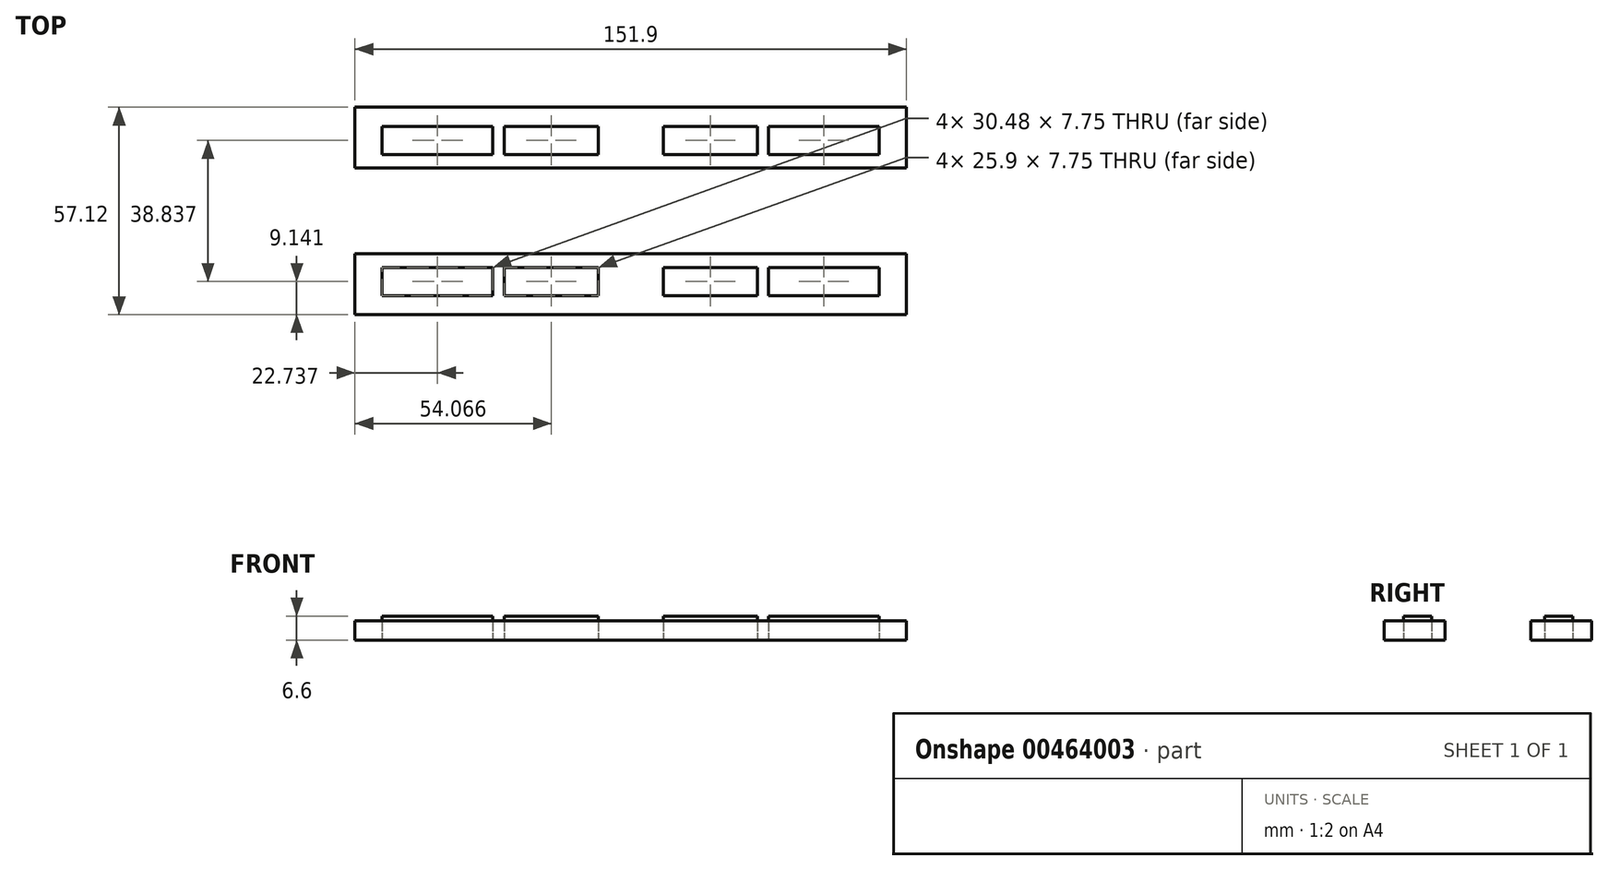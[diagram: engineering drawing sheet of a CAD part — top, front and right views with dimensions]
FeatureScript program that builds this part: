
annotation { "Feature Type Name" : "Feature", "Feature Type Description" : "" }
export const myFeature = defineFeature(function(context is Context, id is Id, definition is map)
    precondition{}
    {
        {
            var Q0;
            Q0=qCreatedBy(makeId("Top.planeOp"),FACE);
            var sketch = newSketch(context, id + "F0", { "sketchPlane" : qUnion([Q0])});
            skLineSegment(sketch, "E0", {"start": v(0, 28.56) * mm, "end": v(-75.95, 28.56) * mm});
            skLineSegment(sketch, "E1", {"start": v(0, 28.56) * mm, "end": v(75.95, 28.56) * mm});
            skLineSegment(sketch, "E2", {"start": v(-75.95, 28.56) * mm, "end": v(-75.95, 11.8) * mm});
            skLineSegment(sketch, "E3.MirrorCS", {"start": v(75.95, 28.56) * mm, "end": v(75.95, 11.8) * mm});
            skLineSegment(sketch, "E4", {"start": v(-75.95, 11.8) * mm, "end": v(0, 11.8) * mm});
            skLineSegment(sketch, "E5", {"start": v(0, 11.8) * mm, "end": v(75.95, 11.8) * mm});
            skLineSegment(sketch, "E6", {"start": v(-68.45, 20.18) * mm, "end": v(-68.45, 23.3) * mm});
            skPoint(sketch, "E6.startSnap0", {"position": v(-75.95, 20.18) * mm});
            skLineSegment(sketch, "E7", {"start": v(-68.45, 23.3) * mm, "end": v(-68.45, 15.54) * mm});
            skLineSegment(sketch, "E8.MirrorCS", {"start": v(68.45, 23.3) * mm, "end": v(68.45, 15.54) * mm});
            skLineSegment(sketch, "E9", {"start": v(-68.45, 23.3) * mm, "end": v(-37.97, 23.3) * mm});
            skLineSegment(sketch, "E10", {"start": v(-37.97, 15.54) * mm, "end": v(-68.45, 15.54) * mm});
            skPoint(sketch, "E11", {"position": v(-37.97, 23.3) * mm});
            skPoint(sketch, "E11.positionSnap0", {"position": v(-37.97, 28.56) * mm});
            skPoint(sketch, "E12", {"position": v(-37.97, 15.54) * mm});
            skPoint(sketch, "E12.positionSnap0", {"position": v(-37.97, 11.8) * mm});
            skLineSegment(sketch, "E13", {"start": v(-37.97, 23.3) * mm, "end": v(-37.97, 15.54) * mm});
            skLineSegment(sketch, "E14.MirrorCS", {"start": v(37.97, 23.3) * mm, "end": v(37.97, 15.54) * mm});
            skLineSegment(sketch, "E15.MirrorCS", {"start": v(68.45, 23.3) * mm, "end": v(37.97, 23.3) * mm});
            skLineSegment(sketch, "E16.MirrorCS", {"start": v(37.97, 15.54) * mm, "end": v(68.45, 15.54) * mm});
            skLineSegment(sketch, "E17", {"start": v(-0.25, 15.54) * mm, "end": v(0.25, 15.54) * mm});
            skLineSegment(sketch, "E18", {"start": v(0.25, 23.3) * mm, "end": v(-0.25, 23.3) * mm});
            skLineSegment(sketch, "E19.MirrorCS", {"start": v(0.25, 15.54) * mm, "end": v(-0.25, 15.54) * mm});
            skLineSegment(sketch, "E20.MirrorCS", {"start": v(-0.25, 23.3) * mm, "end": v(0.25, 23.3) * mm});
            skPoint(sketch, "E21.orphan", {"position": v(30.23, 23.3) * mm});
            skPoint(sketch, "E22.orphan", {"position": v(30.23, 15.54) * mm});
            skPoint(sketch, "E23.end.orphan", {"position": v(-30.23, 15.54) * mm});
            skPoint(sketch, "E23.start.orphan", {"position": v(-30.23, 23.3) * mm});
            skLineSegment(sketch, "E24", {"start": v(-34.83, 23.3) * mm, "end": v(-34.83, 15.54) * mm});
            skLineSegment(sketch, "E25", {"start": v(-34.83, 15.54) * mm, "end": v(-8.94, 15.54) * mm});
            skLineSegment(sketch, "E26", {"start": v(-8.94, 15.54) * mm, "end": v(-8.94, 23.3) * mm});
            skLineSegment(sketch, "E27", {"start": v(-8.94, 23.3) * mm, "end": v(-34.83, 23.3) * mm});
            skLineSegment(sketch, "E28.MirrorCS", {"start": v(8.94, 15.54) * mm, "end": v(8.94, 23.3) * mm});
            skLineSegment(sketch, "E29.MirrorCS", {"start": v(34.83, 15.54) * mm, "end": v(8.94, 15.54) * mm});
            skLineSegment(sketch, "E30.MirrorCS", {"start": v(34.83, 23.3) * mm, "end": v(34.83, 15.54) * mm});
            skLineSegment(sketch, "E31.MirrorCS", {"start": v(8.94, 23.3) * mm, "end": v(34.83, 23.3) * mm});
            skLineSegment(sketch, "E32.MirrorCS", {"start": v(-75.95, -11.8) * mm, "end": v(0, -11.8) * mm});
            skLineSegment(sketch, "E33.MirrorCS", {"start": v(0, -11.8) * mm, "end": v(75.95, -11.8) * mm});
            skLineSegment(sketch, "E34.MirrorCS", {"start": v(34.83, -15.54) * mm, "end": v(8.94, -15.54) * mm});
            skLineSegment(sketch, "E35.MirrorCS", {"start": v(37.97, -15.54) * mm, "end": v(68.45, -15.54) * mm});
            skLineSegment(sketch, "E36.MirrorCS", {"start": v(-0.25, -23.3) * mm, "end": v(0.25, -23.3) * mm});
            skLineSegment(sketch, "E37.MirrorCS", {"start": v(-0.25, -15.54) * mm, "end": v(0.25, -15.54) * mm});
            skLineSegment(sketch, "E38.MirrorCS", {"start": v(0.25, -15.54) * mm, "end": v(-0.25, -15.54) * mm});
            skLineSegment(sketch, "E39.MirrorCS", {"start": v(0.25, -23.3) * mm, "end": v(-0.25, -23.3) * mm});
            skPoint(sketch, "E40.MirrorP", {"position": v(30.23, -23.3) * mm});
            skLineSegment(sketch, "E41.MirrorCS", {"start": v(68.45, -23.3) * mm, "end": v(68.45, -15.54) * mm});
            skLineSegment(sketch, "E42.MirrorCS", {"start": v(-37.97, -23.3) * mm, "end": v(-37.97, -15.54) * mm});
            skLineSegment(sketch, "E43.MirrorCS", {"start": v(-68.45, -20.18) * mm, "end": v(-68.45, -23.3) * mm});
            skLineSegment(sketch, "E44.MirrorCS", {"start": v(-68.45, -23.3) * mm, "end": v(-68.45, -15.54) * mm});
            skLineSegment(sketch, "E45.MirrorCS", {"start": v(-34.83, -23.3) * mm, "end": v(-34.83, -15.54) * mm});
            skPoint(sketch, "E46.MirrorP", {"position": v(30.23, -15.54) * mm});
            skPoint(sketch, "E47.MirrorP", {"position": v(-37.97, -23.3) * mm});
            skLineSegment(sketch, "E48.MirrorCS", {"start": v(-8.94, -15.54) * mm, "end": v(-8.94, -23.3) * mm});
            skLineSegment(sketch, "E49.MirrorCS", {"start": v(34.83, -23.3) * mm, "end": v(34.83, -15.54) * mm});
            skPoint(sketch, "E50.MirrorP", {"position": v(-37.97, -15.54) * mm});
            skLineSegment(sketch, "E51.MirrorCS", {"start": v(68.45, -23.3) * mm, "end": v(37.97, -23.3) * mm});
            skLineSegment(sketch, "E52.MirrorCS", {"start": v(8.94, -15.54) * mm, "end": v(8.94, -23.3) * mm});
            skLineSegment(sketch, "E53.MirrorCS", {"start": v(-34.83, -15.54) * mm, "end": v(-8.94, -15.54) * mm});
            skLineSegment(sketch, "E54.MirrorCS", {"start": v(-8.94, -23.3) * mm, "end": v(-34.83, -23.3) * mm});
            skLineSegment(sketch, "E55.MirrorCS", {"start": v(8.94, -23.3) * mm, "end": v(34.83, -23.3) * mm});
            skLineSegment(sketch, "E56.MirrorCS", {"start": v(37.97, -23.3) * mm, "end": v(37.97, -15.54) * mm});
            skPoint(sketch, "E57.MirrorP", {"position": v(-30.23, -23.3) * mm});
            skPoint(sketch, "E58.MirrorP", {"position": v(-75.95, -20.18) * mm});
            skLineSegment(sketch, "E59.MirrorCS", {"start": v(-37.97, -15.54) * mm, "end": v(-68.45, -15.54) * mm});
            skPoint(sketch, "E60.MirrorP", {"position": v(-30.23, -15.54) * mm});
            skLineSegment(sketch, "E61.MirrorCS", {"start": v(-68.45, -23.3) * mm, "end": v(-37.97, -23.3) * mm});
            skLineSegment(sketch, "E62.MirrorCS", {"start": v(-75.95, -28.56) * mm, "end": v(-75.95, -11.8) * mm});
            skPoint(sketch, "E63.MirrorP", {"position": v(-37.97, -11.8) * mm});
            skPoint(sketch, "E64.MirrorP", {"position": v(-37.97, -28.56) * mm});
            skLineSegment(sketch, "E65.MirrorCS", {"start": v(0, -28.56) * mm, "end": v(75.95, -28.56) * mm});
            skLineSegment(sketch, "E66.MirrorCS", {"start": v(75.95, -28.56) * mm, "end": v(75.95, -11.8) * mm});
            skLineSegment(sketch, "E67.MirrorCS", {"start": v(0, -28.56) * mm, "end": v(-75.95, -28.56) * mm});
            skSolve(sketch);
        }
        {
            var Q0;
            Q0 = qSketchRegion(id + "F0", true);
            extrude(context, id + "F1", {"entities" : qUnion([Q0]), "depth" : 5.33 * mm});
        }
        {
            var Q0;
            {var subQ1=sQuery(id+"F0.wireOp",EDGE,"E9");Q0=makeQuery(id+"F0.imprint","IMPRINT",FACE,{"disambiguationData":[TD([[makeQuery(id+"F0.imprint","IMPRINT",EDGE,{"derivedFrom":subQ1}),-1.0]])]});}
            var Q1;
            Q1=makeQuery(id+"F0.imprint","IMPRINT",FACE,{"disambiguationData":[TD([[makeQuery(id+"F0.imprint","IMPRINT",EDGE,{"derivedFrom":sQuery(id+"F0.wireOp",EDGE,"E24")}),1.0]])]});
            var Q2;
            Q2=makeQuery(id+"F0.imprint","IMPRINT",FACE,{"disambiguationData":[TD([[makeQuery(id+"F0.imprint","IMPRINT",EDGE,{"derivedFrom":sQuery(id+"F0.wireOp",EDGE,"E28.MirrorCS")}),-1.0]])]});
            var Q3;
            Q3=makeQuery(id+"F0.imprint","IMPRINT",FACE,{"disambiguationData":[TD([[makeQuery(id+"F0.imprint","IMPRINT",EDGE,{"derivedFrom":sQuery(id+"F0.wireOp",EDGE,"E14.MirrorCS")}),1.0]])]});
            var Q4;
            Q4=makeQuery(id+"F0.imprint","IMPRINT",FACE,{"disambiguationData":[TD([[makeQuery(id+"F0.imprint","IMPRINT",EDGE,{"derivedFrom":sQuery(id+"F0.wireOp",EDGE,"E42.MirrorCS")}),1.0]])]});
            var Q5;
            Q5=makeQuery(id+"F0.imprint","IMPRINT",FACE,{"disambiguationData":[TD([[makeQuery(id+"F0.imprint","IMPRINT",EDGE,{"derivedFrom":sQuery(id+"F0.wireOp",EDGE,"E45.MirrorCS")}),-1.0]])]});
            var Q6;
            Q6=makeQuery(id+"F0.imprint","IMPRINT",FACE,{"disambiguationData":[TD([[makeQuery(id+"F0.imprint","IMPRINT",EDGE,{"derivedFrom":sQuery(id+"F0.wireOp",EDGE,"E49.MirrorCS")}),1.0]])]});
            var Q7;
            Q7=makeQuery(id+"F0.imprint","IMPRINT",FACE,{"disambiguationData":[TD([[makeQuery(id+"F0.imprint","IMPRINT",EDGE,{"derivedFrom":sQuery(id+"F0.wireOp",EDGE,"E51.MirrorCS")}),-1.0]])]});
            extrude(context, id + "F2", {"entities" : qUnion([Q0, Q1, Q2, Q3, Q4, Q5, Q6, Q7]), "depth" : 6.6 * mm});
        }
    });
